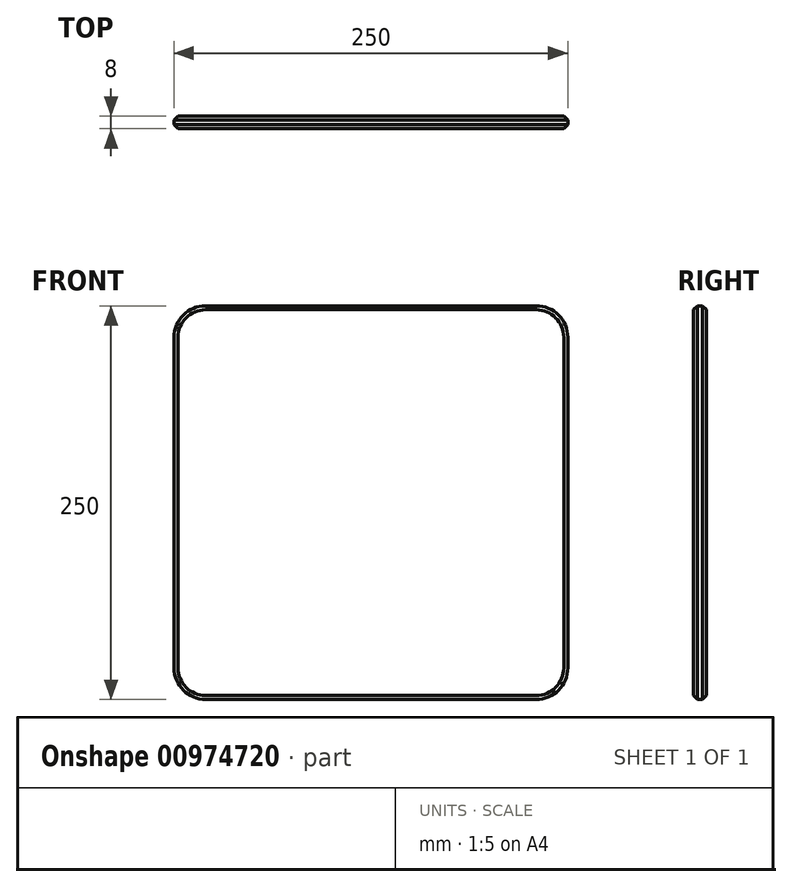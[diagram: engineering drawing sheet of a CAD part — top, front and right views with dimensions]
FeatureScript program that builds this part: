
annotation { "Feature Type Name" : "Feature", "Feature Type Description" : "" }
export const myFeature = defineFeature(function(context is Context, id is Id, definition is map)
    precondition{}
    {
        {
            var Q0;
            Q0=qCreatedBy(makeId("Front.planeOp"),FACE);
            var sketch = newSketch(context, id + "F0", { "sketchPlane" : qUnion([Q0])});
            skLineSegment(sketch, "E0.bottom", {"start": v(-119.18, 138.3) * mm, "end": v(130.82, 138.3) * mm});
            skLineSegment(sketch, "E0.top", {"start": v(-119.18, -111.7) * mm, "end": v(130.82, -111.7) * mm});
            skLineSegment(sketch, "E0.left", {"start": v(-119.18, 138.3) * mm, "end": v(-119.18, -111.7) * mm});
            skLineSegment(sketch, "E0.right", {"start": v(130.82, 138.3) * mm, "end": v(130.82, -111.7) * mm});
            skSolve(sketch);
        }
        {
            var Q0;
            Q0=makeQuery(id+"F0.imprint","IMPRINT",FACE,{"disambiguationData":[TD([[makeQuery(id+"F0.imprint","IMPRINT",EDGE,{"derivedFrom":sQuery(id+"F0.wireOp",EDGE,"E0.bottom")}),-1.0]])]});
            extrude(context, id + "F1", {"entities" : qUnion([Q0]), "depth" : 8 * mm, "offsetDistance" : 25 * mm});
        }
        {
            var Q0;
            Q0=makeQuery(id+"F1.opExtrude","SWEPT_EDGE",EDGE,{"disambiguationData":[OSD([sQuery(id+"F0.wireOp",EDGE,"E0.top"),sQuery(id+"F0.wireOp",EDGE,"E0.left")])]});
            var Q1;
            Q1=makeQuery(id+"F1.opExtrude","SWEPT_EDGE",EDGE,{"disambiguationData":[OSD([sQuery(id+"F0.wireOp",EDGE,"E0.top"),sQuery(id+"F0.wireOp",EDGE,"E0.right")])]});
            var Q2;
            Q2=makeQuery(id+"F1.opExtrude","SWEPT_EDGE",EDGE,{"disambiguationData":[OSD([sQuery(id+"F0.wireOp",EDGE,"E0.bottom"),sQuery(id+"F0.wireOp",EDGE,"E0.right")])]});
            var Q3;
            Q3=makeQuery(id+"F1.opExtrude","SWEPT_EDGE",EDGE,{"disambiguationData":[OSD([sQuery(id+"F0.wireOp",EDGE,"E0.bottom"),sQuery(id+"F0.wireOp",EDGE,"E0.left")])]});
            fillet(context, id + "F2", {"entities" : qUnion([Q0, Q1, Q2, Q3]), "radius" : 20 * mm, "tangentPropagation" : true, "allowEdgeOverflow" : false});
        }
        {
            var Q0;
            Q0=makeQuery(id+"F1.opExtrude","CAP_EDGE",EDGE,{"disambiguationData":[OSD([sQuery(id+"F0.wireOp",EDGE,"E0.top")])],"isStart":true});
            var Q1;
            {var subQ0=sQuery(id+"F0.wireOp",EDGE,"E0.left");var subQ1=sQuery(id+"F0.wireOp",EDGE,"E0.top");Q1=makeQuery(id+"F2.opFillet","BLEND_EDGE",EDGE,{"blendedFrom":[makeQuery(id+"F1.opExtrude","SWEPT_EDGE",EDGE,{"disambiguationData":[OSD([subQ1,subQ0])]}),makeQuery(id+"F1.opExtrude","CAP_FACE",FACE,{"disambiguationData":[OSD([sQuery(id+"F0.wireOp",EDGE,"E0.bottom"),subQ1,subQ0,sQuery(id+"F0.wireOp",EDGE,"E0.right")])],"isStart":true})],"blendedInto":[makeQuery(id+"F1.opExtrude","CAP_FACE",FACE,{"disambiguationData":[OSD([sQuery(id+"F0.wireOp",EDGE,"E0.bottom"),subQ1,subQ0,sQuery(id+"F0.wireOp",EDGE,"E0.right")])],"isStart":true})]});}
            var Q2;
            Q2=makeQuery(id+"F1.opExtrude","CAP_EDGE",EDGE,{"disambiguationData":[OSD([sQuery(id+"F0.wireOp",EDGE,"E0.left")])],"isStart":true});
            var Q3;
            {var subQ0=sQuery(id+"F0.wireOp",EDGE,"E0.left");var subQ1=sQuery(id+"F0.wireOp",EDGE,"E0.bottom");Q3=makeQuery(id+"F2.opFillet","BLEND_EDGE",EDGE,{"blendedFrom":[makeQuery(id+"F1.opExtrude","SWEPT_EDGE",EDGE,{"disambiguationData":[OSD([subQ1,subQ0])]}),makeQuery(id+"F1.opExtrude","CAP_FACE",FACE,{"disambiguationData":[OSD([subQ1,sQuery(id+"F0.wireOp",EDGE,"E0.top"),subQ0,sQuery(id+"F0.wireOp",EDGE,"E0.right")])],"isStart":true})],"blendedInto":[makeQuery(id+"F1.opExtrude","CAP_FACE",FACE,{"disambiguationData":[OSD([subQ1,sQuery(id+"F0.wireOp",EDGE,"E0.top"),subQ0,sQuery(id+"F0.wireOp",EDGE,"E0.right")])],"isStart":true})]});}
            var Q4;
            Q4=makeQuery(id+"F1.opExtrude","CAP_FACE",FACE,{"disambiguationData":[OSD([sQuery(id+"F0.wireOp",EDGE,"E0.bottom"),sQuery(id+"F0.wireOp",EDGE,"E0.top"),sQuery(id+"F0.wireOp",EDGE,"E0.left"),sQuery(id+"F0.wireOp",EDGE,"E0.right")])],"isStart":true});
            var Q5;
            {var subQ0=sQuery(id+"F0.wireOp",EDGE,"E0.right");var subQ1=sQuery(id+"F0.wireOp",EDGE,"E0.top");Q5=makeQuery(id+"F2.opFillet","BLEND_EDGE",EDGE,{"blendedFrom":[makeQuery(id+"F1.opExtrude","SWEPT_EDGE",EDGE,{"disambiguationData":[OSD([subQ1,subQ0])]}),makeQuery(id+"F1.opExtrude","CAP_FACE",FACE,{"disambiguationData":[OSD([sQuery(id+"F0.wireOp",EDGE,"E0.bottom"),subQ1,sQuery(id+"F0.wireOp",EDGE,"E0.left"),subQ0])],"isStart":false})],"blendedInto":[makeQuery(id+"F1.opExtrude","CAP_FACE",FACE,{"disambiguationData":[OSD([sQuery(id+"F0.wireOp",EDGE,"E0.bottom"),subQ1,sQuery(id+"F0.wireOp",EDGE,"E0.left"),subQ0])],"isStart":false})]});}
            var Q6;
            Q6=makeQuery(id+"F1.opExtrude","CAP_EDGE",EDGE,{"disambiguationData":[OSD([sQuery(id+"F0.wireOp",EDGE,"E0.top")])],"isStart":false});
            chamfer(context, id + "F3", {"entities" : qUnion([Q0, Q1, Q2, Q3, Q4, Q5, Q6]), "width" : 2.5 * mm, "tangentPropagation" : true});
        }
    });
